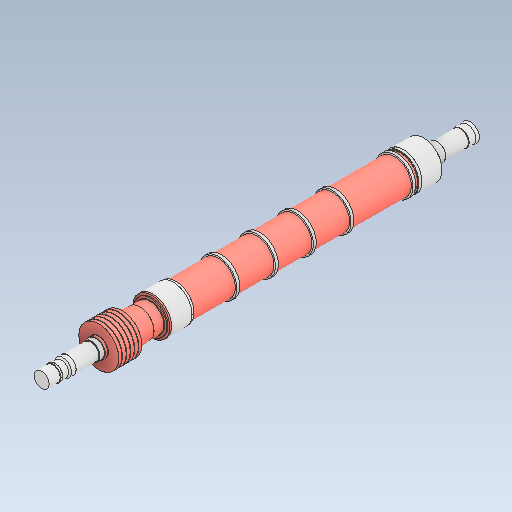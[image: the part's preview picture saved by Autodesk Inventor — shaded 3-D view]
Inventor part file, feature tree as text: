
AUTODESK INVENTOR PART (.ipt)
format: ipt  version: 2021 (Build 250183000, 183)  size: 261,120 bytes
history: mixed  units: in
note: dims shown in document units (in); Inventor stores cm internally (conversion verified against a paired STEP export)
features: fillet x1, imported_body x1
ambient origin geometry x8: Origin, YZ Plane, XZ Plane, XY Plane, X Axis, Y Axis, Z Axis, Center Point
bodies: Solid1 (imported_parasolid)
feature tree (2):
  fillet  "Fillet19"  [1 undecoded]
  imported_body  NMx_Import_Brep_tag  [imported B-rep: ~101 faces, bbox_mm=[1147.88315, 0.0, 12704.53136]]
note: 1 required parameter value undecoded (feature->parameter linkage not recoverable at this tier; creation-order binding heuristic only, values carry confidence <= 0.55)
